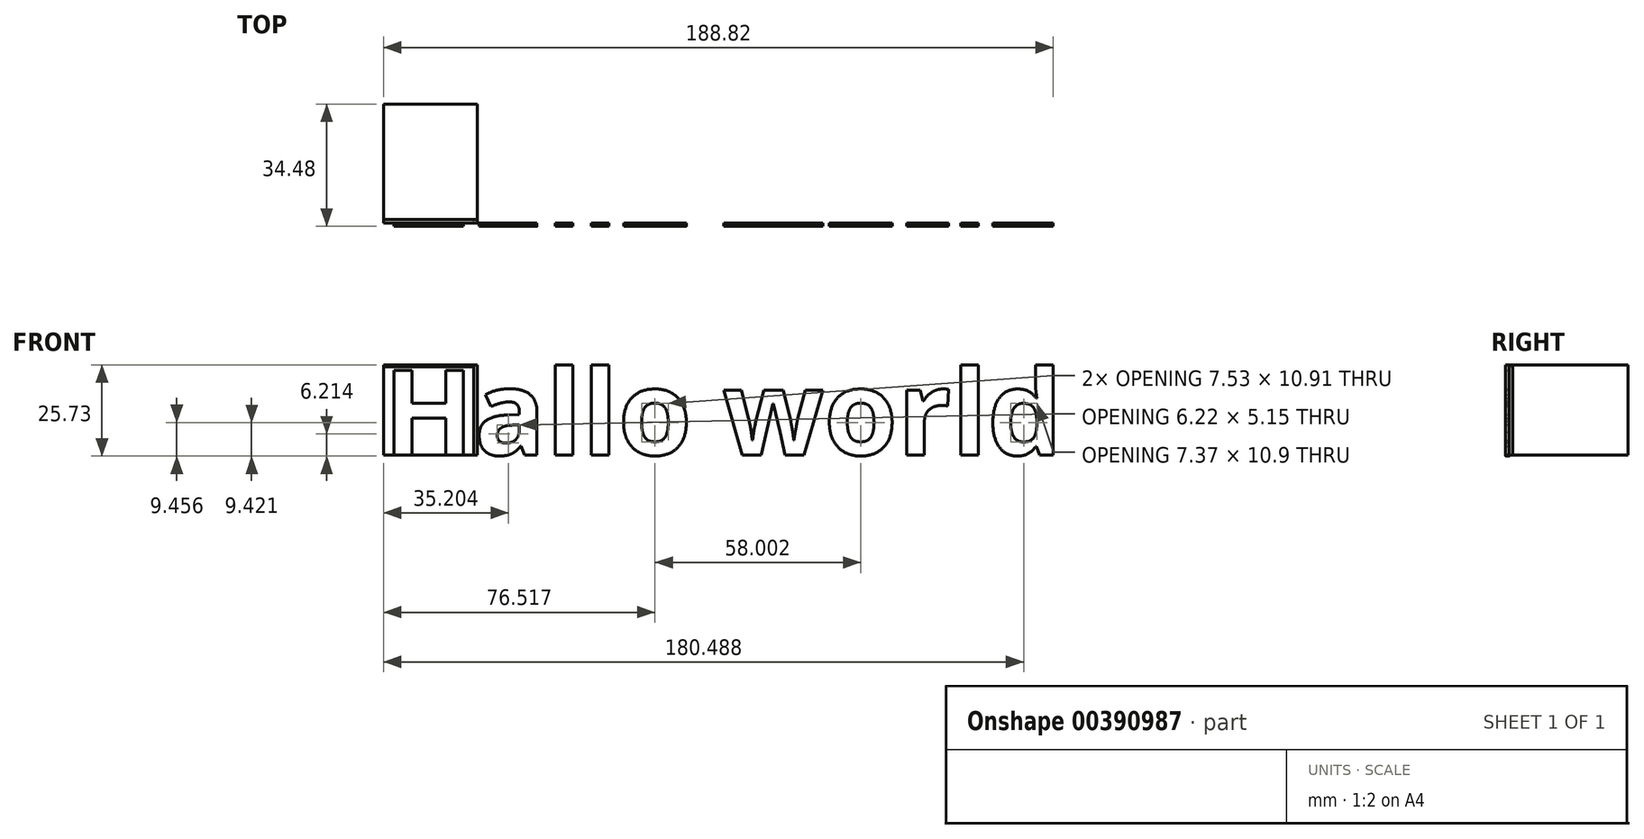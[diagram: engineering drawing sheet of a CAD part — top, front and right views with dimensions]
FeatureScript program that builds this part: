
annotation { "Feature Type Name" : "Feature", "Feature Type Description" : "" }
export const myFeature = defineFeature(function(context is Context, id is Id, definition is map)
    precondition{}
    {
        {
            var Q0;
            Q0=qCreatedBy(makeId("Top.planeOp"),FACE);
            var sketch = newSketch(context, id + "F0", { "sketchPlane" : qUnion([Q0])});
            skLineSegment(sketch, "E0.bottom", {"start": v(0, 0) * mm, "end": v(26.44, 0) * mm});
            skLineSegment(sketch, "E0.top", {"start": v(0, 32.48) * mm, "end": v(26.44, 32.48) * mm});
            skLineSegment(sketch, "E0.left", {"start": v(0, 0) * mm, "end": v(0, 32.48) * mm});
            skLineSegment(sketch, "E0.right", {"start": v(26.44, 0) * mm, "end": v(26.44, 32.48) * mm});
            skSolve(sketch);
        }
        {
            var Q0;
            Q0=makeQuery(id+"F0.imprint","IMPRINT",FACE,{"disambiguationData":[TD([[makeQuery(id+"F0.imprint","IMPRINT",EDGE,{"derivedFrom":sQuery(id+"F0.wireOp",EDGE,"E0.bottom")}),1.0]])]});
            extrude(context, id + "F1", {"entities" : qUnion([Q0]), "depth" : 25.4 * mm});
        }
        {
            var Q0;
            Q0=makeQuery(id+"F1.opExtrude","SWEPT_FACE",FACE,{"disambiguationData":[OSD([sQuery(id+"F0.wireOp",EDGE,"E0.bottom")])]});
            var sketch = newSketch(context, id + "F2", { "sketchPlane" : qUnion([Q0])});
            skSolve(sketch);
        }
        {
            var Q0;
            Q0=qSketchRegion(id+"F2",true);
            var Q1;
            {var subQ0=sQuery(id+"F0.wireOp",EDGE,"E0.bottom");Q1=makeQuery(id+"F2.imprint","IMPRINT",FACE,{"disambiguationData":[TD([[makeQuery(id+"F2.imprint","IMPRINT",EDGE,{"derivedFrom":makeQuery(id+"F1.opExtrude","CAP_EDGE",EDGE,{"disambiguationData":[OSD([subQ0])],"isStart":true})}),1.0]])]});}
            var Q2;
            Q2=qSketchRegion(id+"Fvldm2TemygVzHW_1",true);
            extrude(context, id + "F3", {"entities" : qUnion([Q0, Q1, Q2]), "depth" : 1 * mm});
        }
        {
            var Q0;
            Q0=makeQuery(id+"F3.opExtrude","CAP_FACE",FACE,{"disambiguationData":[OSD([sQuery(id+"F0.wireOp",EDGE,"E0.bottom"),sQuery(id+"F0.wireOp",EDGE,"E0.left"),sQuery(id+"F0.wireOp",EDGE,"E0.right")])],"isStart":false});
            var sketch = newSketch(context, id + "F4", { "sketchPlane" : qUnion([Q0])});
            skSolve(sketch);
        }
        {
            var Q0;
            {var subQ0=sQuery(id+"F0.wireOp",EDGE,"E0.bottom");Q0=makeQuery(id+"F4.imprint","IMPRINT",FACE,{"disambiguationData":[TD([[makeQuery(id+"F4.imprint","IMPRINT",EDGE,{"derivedFrom":makeQuery(id+"F3.opExtrude","CAP_EDGE",EDGE,{"disambiguationData":[OSD([subQ0]),TDD([makeQuery(id+"F2.imprint","IMPRINT",EDGE,{"derivedFrom":makeQuery(id+"F1.opExtrude","CAP_EDGE",EDGE,{"disambiguationData":[OSD([subQ0])],"isStart":true})})])],"isStart":false})}),1.0]])]});}
            var sketch = newSketch(context, id + "F5", { "sketchPlane" : qUnion([Q0])});
            skText(sketch, "E1", { "text": "Hallo world", "fontName": "OpenSans-Bold.ttf"});
            const initialGuessF5  = {"E1": [0, 0, 1, 0, 0.02407]};
            skSetInitialGuess(sketch, initialGuessF5);
            skSolve(sketch);
        }
        {
            var Q0;
            Q0=qCreatedBy(makeId("Front.planeOp"),FACE);
            var sketch = newSketch(context, id + "F6", { "sketchPlane" : qUnion([Q0])});
            skLineSegment(sketch, "E2.bottom", {"start": v(0, 0) * mm, "end": v(25.48, 0) * mm});
            skLineSegment(sketch, "E2.top", {"start": v(0, 24.84) * mm, "end": v(25.48, 24.84) * mm});
            skLineSegment(sketch, "E2.left", {"start": v(0, 0) * mm, "end": v(0, 24.84) * mm});
            skLineSegment(sketch, "E2.right", {"start": v(25.48, 0) * mm, "end": v(25.48, 24.84) * mm});
            skSolve(sketch);
        }
        {
            var Q0;
            Q0=qSketchRegion(id+"F6",true);
            var Q1;
            Q1=qSketchRegion(id+"F5",true);
            extrude(context, id + "F7", {"entities" : qUnion([Q0, Q1]), "depth" : 1 * mm});
        }
    });
